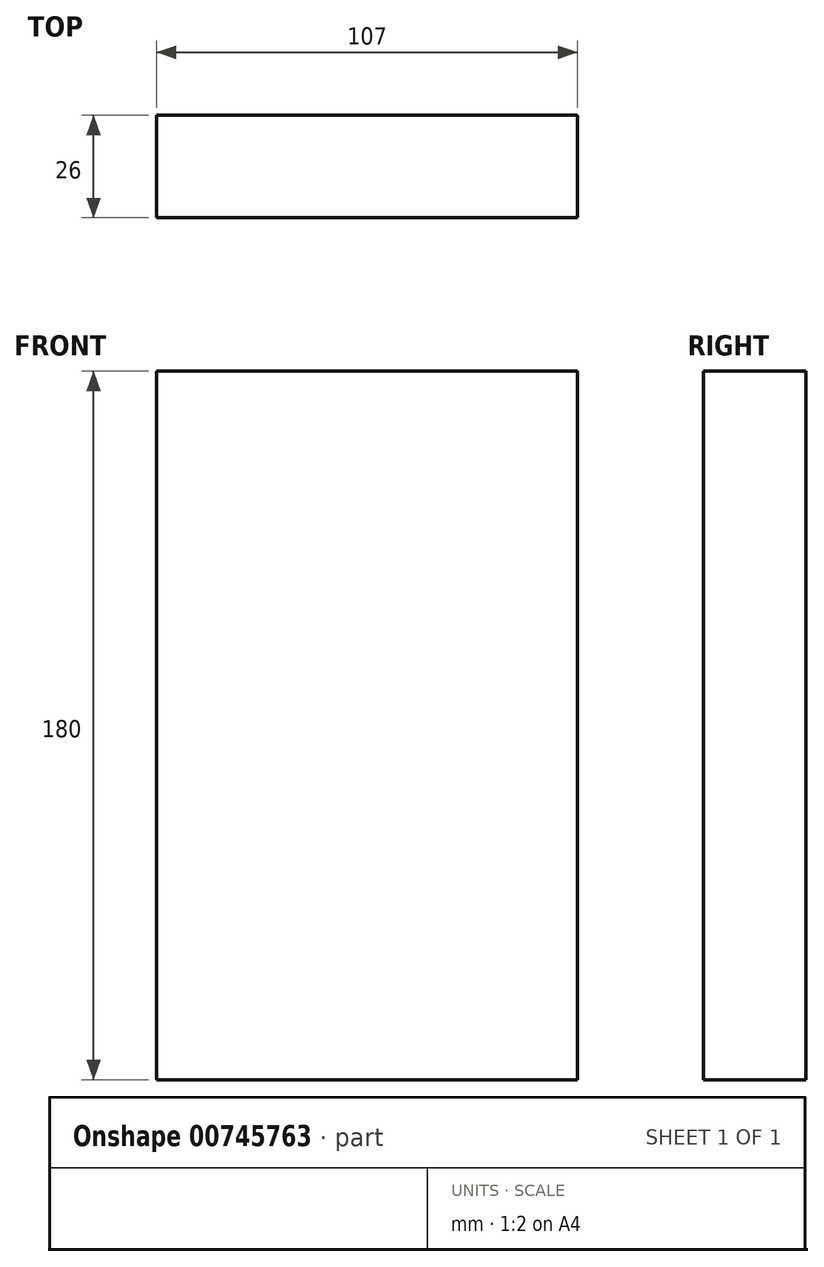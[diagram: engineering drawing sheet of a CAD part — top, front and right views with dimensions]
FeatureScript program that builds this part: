
annotation { "Feature Type Name" : "Feature", "Feature Type Description" : "" }
export const myFeature = defineFeature(function(context is Context, id is Id, definition is map)
    precondition{}
    {
        {
            var Q0;
            Q0=qCreatedBy(makeId("Front.planeOp"),FACE);
            var sketch = newSketch(context, id + "F0", { "sketchPlane" : qUnion([Q0])});
            skLineSegment(sketch, "E0.bottom", {"start": v(-53.5, 90) * mm, "end": v(53.5, 90) * mm});
            skLineSegment(sketch, "E0.top", {"start": v(-53.5, -90) * mm, "end": v(53.5, -90) * mm});
            skLineSegment(sketch, "E0.left", {"start": v(-53.5, 90) * mm, "end": v(-53.5, -90) * mm});
            skLineSegment(sketch, "E0.right", {"start": v(53.5, 90) * mm, "end": v(53.5, -90) * mm});
            skPoint(sketch, "E0.middle", {"position": v(0, 0) * mm});
            skSolve(sketch);
        }
        {
            var Q0;
            Q0=makeQuery(id+"F0.imprint","IMPRINT",FACE,{"disambiguationData":[TD([[makeQuery(id+"F0.imprint","IMPRINT",EDGE,{"derivedFrom":sQuery(id+"F0.wireOp",EDGE,"E0.bottom")}),-1.0]])]});
            extrude(context, id + "F1", {"entities" : qUnion([Q0]), "depth" : 26 * mm, "offsetDistance" : 25 * mm});
        }
    });
